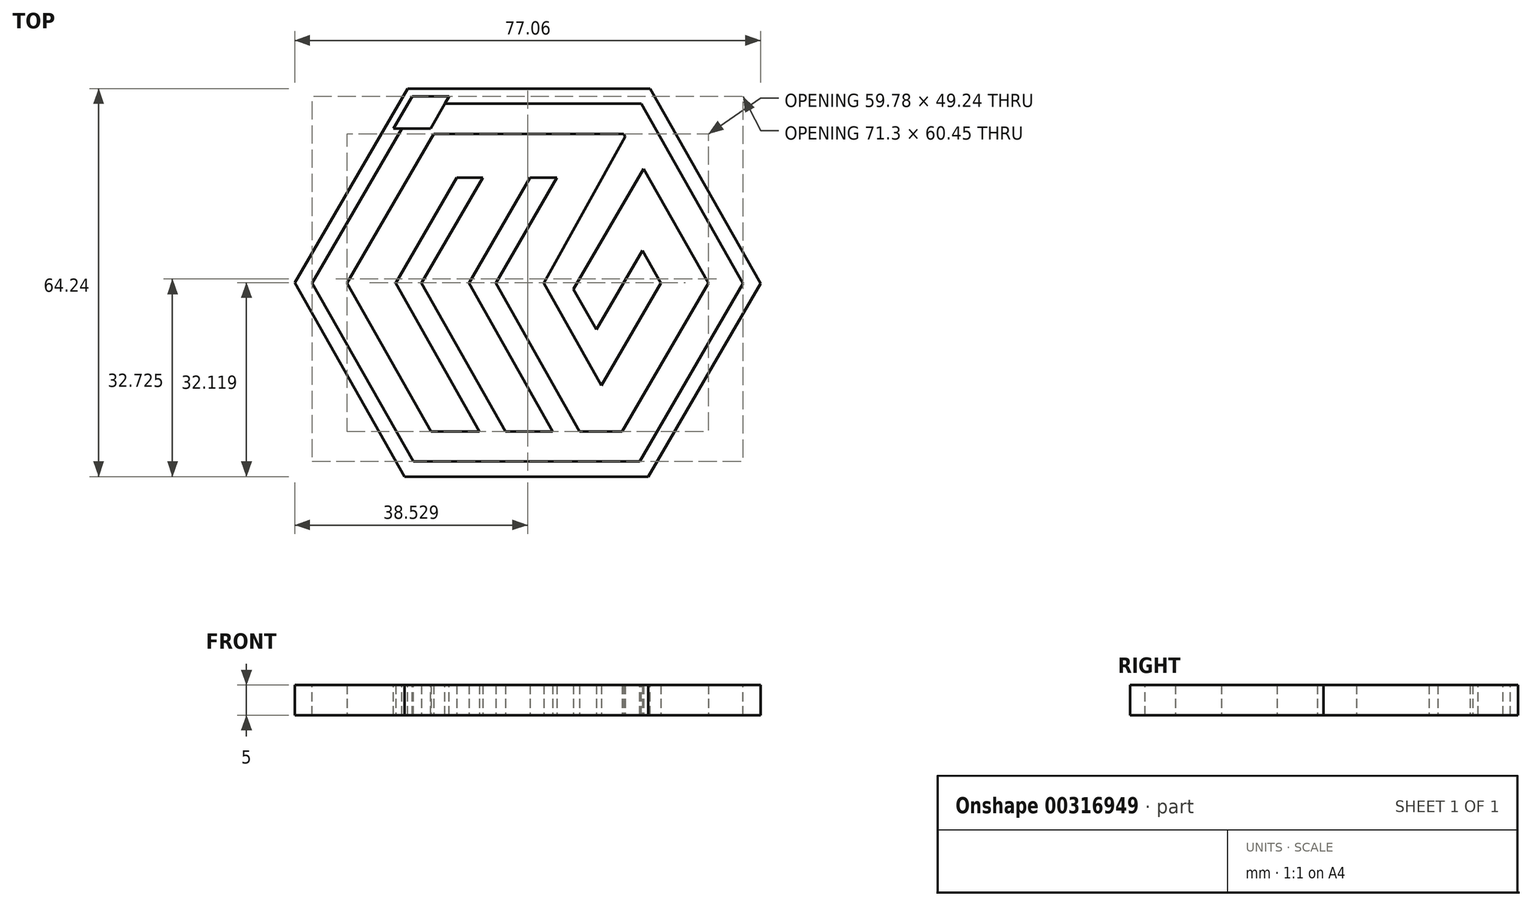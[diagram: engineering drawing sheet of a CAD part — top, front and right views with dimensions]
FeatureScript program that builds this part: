
annotation { "Feature Type Name" : "Feature", "Feature Type Description" : "" }
export const myFeature = defineFeature(function(context is Context, id is Id, definition is map)
    precondition{}
    {
        {
            var Q0;
            Q0=qCreatedBy(makeId("Top.planeOp"),FACE);
            var sketch = newSketch(context, id + "F0", { "sketchPlane" : qUnion([Q0])});
            skPoint(sketch, "E0.start.orphan", {"position": v(-29.22, 0) * mm});
            skLineSegment(sketch, "E1", {"start": v(16.8, -24.54) * mm, "end": v(31.04, 0) * mm});
            skLineSegment(sketch, "E2", {"start": v(31.04, 0) * mm, "end": v(20.32, 18.93) * mm});
            skLineSegment(sketch, "E3", {"start": v(8.75, -1) * mm, "end": v(12.53, -7.68) * mm});
            skLineSegment(sketch, "E4", {"start": v(12.53, -7.68) * mm, "end": v(20.13, 5.42) * mm});
            skLineSegment(sketch, "E5", {"start": v(20.13, 5.42) * mm, "end": v(23.2, 0) * mm});
            skLineSegment(sketch, "E6", {"start": v(23.2, 0) * mm, "end": v(13.38, -16.92) * mm});
            skLineSegment(sketch, "E7", {"start": v(13.38, -16.92) * mm, "end": v(3.8, 0) * mm});
            skLineSegment(sketch, "E8", {"start": v(18.14, 24.7) * mm, "end": v(-14.4, 24.7) * mm});
            skLineSegment(sketch, "E9", {"start": v(-14.4, 24.7) * mm, "end": v(-28.74, 0) * mm});
            skLineSegment(sketch, "E10", {"start": v(-28.74, 0) * mm, "end": v(-14.85, -24.54) * mm});
            skLineSegment(sketch, "E11", {"start": v(-14.85, -24.54) * mm, "end": v(-6.81, -24.54) * mm});
            skLineSegment(sketch, "E12", {"start": v(-6.81, -24.54) * mm, "end": v(-20.7, 0) * mm});
            skLineSegment(sketch, "E13", {"start": v(-20.7, 0) * mm, "end": v(-10.58, 17.44) * mm});
            skLineSegment(sketch, "E14", {"start": v(-10.58, 17.44) * mm, "end": v(-6.3, 17.44) * mm});
            skLineSegment(sketch, "E15", {"start": v(-6.3, 17.44) * mm, "end": v(-16.42, 0) * mm});
            skLineSegment(sketch, "E16", {"start": v(-16.42, 0) * mm, "end": v(-2.53, -24.54) * mm});
            skLineSegment(sketch, "E17", {"start": v(-2.53, -24.54) * mm, "end": v(5.3, -24.54) * mm});
            skLineSegment(sketch, "E18", {"start": v(5.3, -24.54) * mm, "end": v(-8.58, 0) * mm});
            skLineSegment(sketch, "E19", {"start": v(-8.58, 0) * mm, "end": v(1.54, 17.44) * mm});
            skLineSegment(sketch, "E20", {"start": v(1.54, 17.44) * mm, "end": v(6, 17.44) * mm});
            skLineSegment(sketch, "E21", {"start": v(6, 17.44) * mm, "end": v(-4.13, 0) * mm});
            skLineSegment(sketch, "E22", {"start": v(-4.13, 0) * mm, "end": v(9.76, -24.54) * mm});
            skLineSegment(sketch, "E23", {"start": v(9.76, -24.54) * mm, "end": v(16.8, -24.54) * mm});
            skPoint(sketch, "E24.end.orphan", {"position": v(17.06, 24.7) * mm});
            skLineSegment(sketch, "E25", {"start": v(17.31, 24.25) * mm, "end": v(3.8, 0) * mm});
            skLineSegment(sketch, "E26", {"start": v(20.32, 18.93) * mm, "end": v(17.06, 24.7) * mm});
            skLineSegment(sketch, "E27", {"start": v(20.32, 18.93) * mm, "end": v(8.75, -1) * mm});
            skSolve(sketch);
        }
        {
            var Q0;
            Q0=makeQuery(id+"F0.imprint","IMPRINT",FACE,{"disambiguationData":[TD([[makeQuery(id+"F0.imprint","IMPRINT",EDGE,{"derivedFrom":sQuery(id+"F0.wireOp",EDGE,"E1")}),1.0]])]});
            extrude(context, id + "F1", {"entities" : qUnion([Q0]), "depth" : 5 * mm});
        }
        {
            var Q0;
            Q0=makeQuery(id+"F1.opExtrude","CAP_FACE",FACE,{"disambiguationData":[OSD([sQuery(id+"F0.wireOp",EDGE,"E1"),sQuery(id+"F0.wireOp",EDGE,"E2"),sQuery(id+"F0.wireOp",EDGE,"dDSeGD3p-nWlW-Dyv2-dVy7-jL1SRDRqiARk"),sQuery(id+"F0.wireOp",EDGE,"E3"),sQuery(id+"F0.wireOp",EDGE,"E4"),sQuery(id+"F0.wireOp",EDGE,"E5"),sQuery(id+"F0.wireOp",EDGE,"E6"),sQuery(id+"F0.wireOp",EDGE,"E7"),sQuery(id+"F0.wireOp",EDGE,"zCbFyB80-4xBb-39Aw-3cKm-Xl61SkS5O1Jh"),sQuery(id+"F0.wireOp",EDGE,"E8"),sQuery(id+"F0.wireOp",EDGE,"E9"),sQuery(id+"F0.wireOp",EDGE,"E10"),sQuery(id+"F0.wireOp",EDGE,"E11"),sQuery(id+"F0.wireOp",EDGE,"E12"),sQuery(id+"F0.wireOp",EDGE,"E13"),sQuery(id+"F0.wireOp",EDGE,"E14"),sQuery(id+"F0.wireOp",EDGE,"E15"),sQuery(id+"F0.wireOp",EDGE,"E16"),sQuery(id+"F0.wireOp",EDGE,"E17"),sQuery(id+"F0.wireOp",EDGE,"E18"),sQuery(id+"F0.wireOp",EDGE,"E19"),sQuery(id+"F0.wireOp",EDGE,"E20"),sQuery(id+"F0.wireOp",EDGE,"E21"),sQuery(id+"F0.wireOp",EDGE,"E22"),sQuery(id+"F0.wireOp",EDGE,"E23")])],"isStart":false});
            var sketch = newSketch(context, id + "F2", { "sketchPlane" : qUnion([Q0])});
            skLineSegment(sketch, "E28.0", {"start": v(-14.4, 24.7) * mm, "end": v(-14.4, 24.7) * mm});
            skLineSegment(sketch, "E29.0", {"start": v(-17.29, 29.7) * mm, "end": v(-34.5, 0.03) * mm});
            skLineSegment(sketch, "E29.1", {"start": v(19.97, 29.7) * mm, "end": v(36.8, -0.03) * mm});
            skLineSegment(sketch, "E29.2", {"start": v(19.68, -29.54) * mm, "end": v(36.8, -0.03) * mm});
            skLineSegment(sketch, "E29.3", {"start": v(-17.29, 29.7) * mm, "end": v(19.97, 29.7) * mm});
            skLineSegment(sketch, "E29.4", {"start": v(-17.77, -29.54) * mm, "end": v(19.68, -29.54) * mm});
            skLineSegment(sketch, "E29.5", {"start": v(-34.5, 0.03) * mm, "end": v(-17.77, -29.54) * mm});
            skPoint(sketch, "E30.0.start.orphan", {"position": v(-28.74, 0) * mm});
            skPoint(sketch, "E31.start.orphan", {"position": v(-14.85, -24.54) * mm});
            skPoint(sketch, "E32.0.start.orphan", {"position": v(16.8, -24.54) * mm});
            skPoint(sketch, "E33.end.orphan", {"position": v(31.04, 0) * mm});
            skSolve(sketch);
        }
        {
            var Q0;
            Q0 = qSketchRegion(id + "F2", true);
            extrude(context, id + "F3", {"entities" : qUnion([Q0]), "oppositeDirection" : true, "depth" : 5 * mm});
        }
        {
            var Q0;
            Q0=makeQuery(id+"F1.opExtrude","SWEPT_BODY",BODY,{"disambiguationData":[OSD([sQuery(id+"F0.wireOp",EDGE,"E1"),sQuery(id+"F0.wireOp",EDGE,"E2"),sQuery(id+"F0.wireOp",EDGE,"E3"),sQuery(id+"F0.wireOp",EDGE,"E4"),sQuery(id+"F0.wireOp",EDGE,"E5"),sQuery(id+"F0.wireOp",EDGE,"E6"),sQuery(id+"F0.wireOp",EDGE,"E7"),sQuery(id+"F0.wireOp",EDGE,"E8"),sQuery(id+"F0.wireOp",EDGE,"E9"),sQuery(id+"F0.wireOp",EDGE,"E10"),sQuery(id+"F0.wireOp",EDGE,"E11"),sQuery(id+"F0.wireOp",EDGE,"E12"),sQuery(id+"F0.wireOp",EDGE,"E13"),sQuery(id+"F0.wireOp",EDGE,"E14"),sQuery(id+"F0.wireOp",EDGE,"E15"),sQuery(id+"F0.wireOp",EDGE,"E16"),sQuery(id+"F0.wireOp",EDGE,"E17"),sQuery(id+"F0.wireOp",EDGE,"E18"),sQuery(id+"F0.wireOp",EDGE,"E19"),sQuery(id+"F0.wireOp",EDGE,"E20"),sQuery(id+"F0.wireOp",EDGE,"E21"),sQuery(id+"F0.wireOp",EDGE,"E22"),sQuery(id+"F0.wireOp",EDGE,"E23"),sQuery(id+"F0.wireOp",EDGE,"E25"),sQuery(id+"F0.wireOp",EDGE,"E26"),sQuery(id+"F0.wireOp",EDGE,"E27")])]});
            var Q1;
            Q1=makeQuery(id+"F3.opExtrude","SWEPT_BODY",BODY,{"disambiguationData":[OSD([sQuery(id+"F2.wireOp",EDGE,"E29.0"),sQuery(id+"F2.wireOp",EDGE,"E29.1"),sQuery(id+"F2.wireOp",EDGE,"E29.2"),sQuery(id+"F2.wireOp",EDGE,"E29.3"),sQuery(id+"F2.wireOp",EDGE,"E29.4"),sQuery(id+"F2.wireOp",EDGE,"E29.5")])]});
            booleanBodies(context, id + "F4", {"operationType" : BooleanOperationType.SUBTRACTION, "tools" : qUnion([Q0]), "targets" : qUnion([Q1]), "keepTools" : true});
        }
        {
            var Q0;
            Q0=makeQuery(id+"F3.opExtrude","CAP_FACE",FACE,{"disambiguationData":[OSD([sQuery(id+"F2.wireOp",EDGE,"E29.0"),sQuery(id+"F2.wireOp",EDGE,"E29.1"),sQuery(id+"F2.wireOp",EDGE,"E29.2"),sQuery(id+"F2.wireOp",EDGE,"E29.3"),sQuery(id+"F2.wireOp",EDGE,"E29.4"),sQuery(id+"F2.wireOp",EDGE,"E29.5")])],"isStart":true});
            var sketch = newSketch(context, id + "F5", { "sketchPlane" : qUnion([Q0])});
            skLineSegment(sketch, "E34.0", {"start": v(-18.73, 32.2) * mm, "end": v(21.43, 32.2) * mm});
            skLineSegment(sketch, "E34.1", {"start": v(-37.38, 0.05) * mm, "end": v(-19.22, -32.04) * mm});
            skLineSegment(sketch, "E34.2", {"start": v(-19.22, -32.04) * mm, "end": v(21.12, -32.04) * mm});
            skLineSegment(sketch, "E34.3", {"start": v(-18.73, 32.2) * mm, "end": v(-37.38, 0.05) * mm});
            skLineSegment(sketch, "E34.4", {"start": v(21.12, -32.04) * mm, "end": v(39.68, -0.05) * mm});
            skLineSegment(sketch, "E34.5", {"start": v(21.43, 32.2) * mm, "end": v(39.68, -0.05) * mm});
            skLineSegment(sketch, "E35.0", {"start": v(-17.29, 29.7) * mm, "end": v(19.97, 29.7) * mm});
            skLineSegment(sketch, "E36.0", {"start": v(19.97, 29.7) * mm, "end": v(36.8, -0.03) * mm});
            skLineSegment(sketch, "E37.0", {"start": v(19.68, -29.54) * mm, "end": v(36.8, -0.03) * mm});
            skLineSegment(sketch, "E38.0", {"start": v(-17.77, -29.54) * mm, "end": v(19.68, -29.54) * mm});
            skLineSegment(sketch, "E39.0", {"start": v(-34.5, 0.03) * mm, "end": v(-17.77, -29.54) * mm});
            skLineSegment(sketch, "E40.0", {"start": v(-17.29, 29.7) * mm, "end": v(-34.5, 0.03) * mm});
            skSolve(sketch);
        }
        {
            var Q0;
            Q0=makeQuery(id+"F5.imprint","IMPRINT",FACE,{"disambiguationData":[TD([[makeQuery(id+"F5.imprint","IMPRINT",EDGE,{"derivedFrom":sQuery(id+"F5.wireOp",EDGE,"E34.0")}),-1.0]])]});
            var Q1;
            Q1=makeQuery(id+"F1.opExtrude","CAP_FACE",FACE,{"disambiguationData":[OSD([sQuery(id+"F0.wireOp",EDGE,"E1"),sQuery(id+"F0.wireOp",EDGE,"E2"),sQuery(id+"F0.wireOp",EDGE,"E3"),sQuery(id+"F0.wireOp",EDGE,"E4"),sQuery(id+"F0.wireOp",EDGE,"E5"),sQuery(id+"F0.wireOp",EDGE,"E6"),sQuery(id+"F0.wireOp",EDGE,"E7"),sQuery(id+"F0.wireOp",EDGE,"E8"),sQuery(id+"F0.wireOp",EDGE,"E9"),sQuery(id+"F0.wireOp",EDGE,"E10"),sQuery(id+"F0.wireOp",EDGE,"E11"),sQuery(id+"F0.wireOp",EDGE,"E12"),sQuery(id+"F0.wireOp",EDGE,"E13"),sQuery(id+"F0.wireOp",EDGE,"E14"),sQuery(id+"F0.wireOp",EDGE,"E15"),sQuery(id+"F0.wireOp",EDGE,"E16"),sQuery(id+"F0.wireOp",EDGE,"E17"),sQuery(id+"F0.wireOp",EDGE,"E18"),sQuery(id+"F0.wireOp",EDGE,"E19"),sQuery(id+"F0.wireOp",EDGE,"E20"),sQuery(id+"F0.wireOp",EDGE,"E21"),sQuery(id+"F0.wireOp",EDGE,"E22"),sQuery(id+"F0.wireOp",EDGE,"E23"),sQuery(id+"F0.wireOp",EDGE,"E25"),sQuery(id+"F0.wireOp",EDGE,"E26"),sQuery(id+"F0.wireOp",EDGE,"E27")])],"isStart":true});
            extrude(context, id + "F6", {"entities" : qUnion([Q0]), "endBound" : BoundingType.UP_TO_SURFACE, "oppositeDirection" : true, "endBoundEntityFace" : qUnion([Q1]), "depth" : 25 * mm});
        }
        {
            var Q0;
            Q0=makeQuery(id+"F3.opExtrude","CAP_FACE",FACE,{"disambiguationData":[OSD([sQuery(id+"F2.wireOp",EDGE,"E29.0"),sQuery(id+"F2.wireOp",EDGE,"E29.1"),sQuery(id+"F2.wireOp",EDGE,"E29.2"),sQuery(id+"F2.wireOp",EDGE,"E29.3"),sQuery(id+"F2.wireOp",EDGE,"E29.4"),sQuery(id+"F2.wireOp",EDGE,"E29.5")])],"isStart":true});
            var sketch = newSketch(context, id + "F7", { "sketchPlane" : qUnion([Q0])});
            skLineSegment(sketch, "E41", {"start": v(-11.5, 29.7) * mm, "end": v(-17.29, 29.7) * mm});
            skLineSegment(sketch, "E42", {"start": v(-17.29, 29.7) * mm, "end": v(-20.19, 24.7) * mm});
            skPoint(sketch, "E43.0.start.orphan", {"position": v(17.06, 24.7) * mm});
            skLineSegment(sketch, "E44", {"start": v(-19.67, 25.6) * mm, "end": v(-14.92, 25.6) * mm});
            skLineSegment(sketch, "E45.MirrorCS", {"start": v(-12.54, 29.7) * mm, "end": v(-14.92, 25.6) * mm});
            skPoint(sketch, "E46.end.orphan", {"position": v(-15.44, 24.7) * mm});
            skPoint(sketch, "E47.orphan", {"position": v(-14.4, 24.7) * mm});
            skPoint(sketch, "E48.orphan", {"position": v(-13.89, 25.6) * mm});
            skSolve(sketch);
        }
        {
            var Q0;
            Q0=makeQuery(id+"F7.imprint","IMPRINT",FACE,{"disambiguationData":[TD([[makeQuery(id+"F7.imprint","IMPRINT",EDGE,{"derivedFrom":sQuery(id+"F7.wireOp",EDGE,"E46")}),-1.0]])]});
            var Q1;
            {var subQ4=sQuery(id+"F7.wireOp",EDGE,"E44");Q1=makeQuery(id+"F7.imprint","IMPRINT",FACE,{"disambiguationData":[TD([[makeQuery(id+"F7.imprint","IMPRINT",EDGE,{"derivedFrom":subQ4}),1.0]])]});}
            extrude(context, id + "F8", {"entities" : qUnion([Q0, Q1]), "operationType" : NewBodyOperationType.REMOVE, "oppositeDirection" : true, "depth" : 25 * mm});
        }
        {
            var Q0;
            Q0=makeQuery(id+"F6.opExtrude","CAP_FACE",FACE,{"disambiguationData":[OSD([sQuery(id+"F5.wireOp",EDGE,"E34.0"),sQuery(id+"F5.wireOp",EDGE,"E34.1"),sQuery(id+"F5.wireOp",EDGE,"E34.2"),sQuery(id+"F5.wireOp",EDGE,"E34.3"),sQuery(id+"F5.wireOp",EDGE,"E34.4"),sQuery(id+"F5.wireOp",EDGE,"E34.5"),sQuery(id+"F5.wireOp",EDGE,"E35.0"),sQuery(id+"F5.wireOp",EDGE,"E36.0"),sQuery(id+"F5.wireOp",EDGE,"E37.0"),sQuery(id+"F5.wireOp",EDGE,"E38.0"),sQuery(id+"F5.wireOp",EDGE,"E39.0"),sQuery(id+"F5.wireOp",EDGE,"E40.0")])],"isStart":true});
            var sketch = newSketch(context, id + "F9", { "sketchPlane" : qUnion([Q0])});
            skLineSegment(sketch, "E49.0", {"start": v(-19.67, 25.6) * mm, "end": v(-14.92, 25.6) * mm});
            skLineSegment(sketch, "E50.0", {"start": v(-12.54, 29.7) * mm, "end": v(-14.92, 25.6) * mm});
            skLineSegment(sketch, "E51", {"start": v(-19.67, 25.6) * mm, "end": v(-21.07, 25.6) * mm});
            skLineSegment(sketch, "E52", {"start": v(-21.07, 25.6) * mm, "end": v(-17.98, 30.91) * mm});
            skLineSegment(sketch, "E53.MirrorCS", {"start": v(-11.83, 30.91) * mm, "end": v(-17.98, 30.91) * mm});
            skLineSegment(sketch, "E54", {"start": v(-12.54, 29.7) * mm, "end": v(-11.83, 30.91) * mm});
            skSolve(sketch);
        }
        {
            var Q0;
            Q0 = qSketchRegion(id + "F9", true);
            extrude(context, id + "F10", {"entities" : qUnion([Q0]), "operationType" : NewBodyOperationType.REMOVE, "oppositeDirection" : true, "depth" : 25 * mm, "offsetDistance" : 25 * mm});
        }
    });
